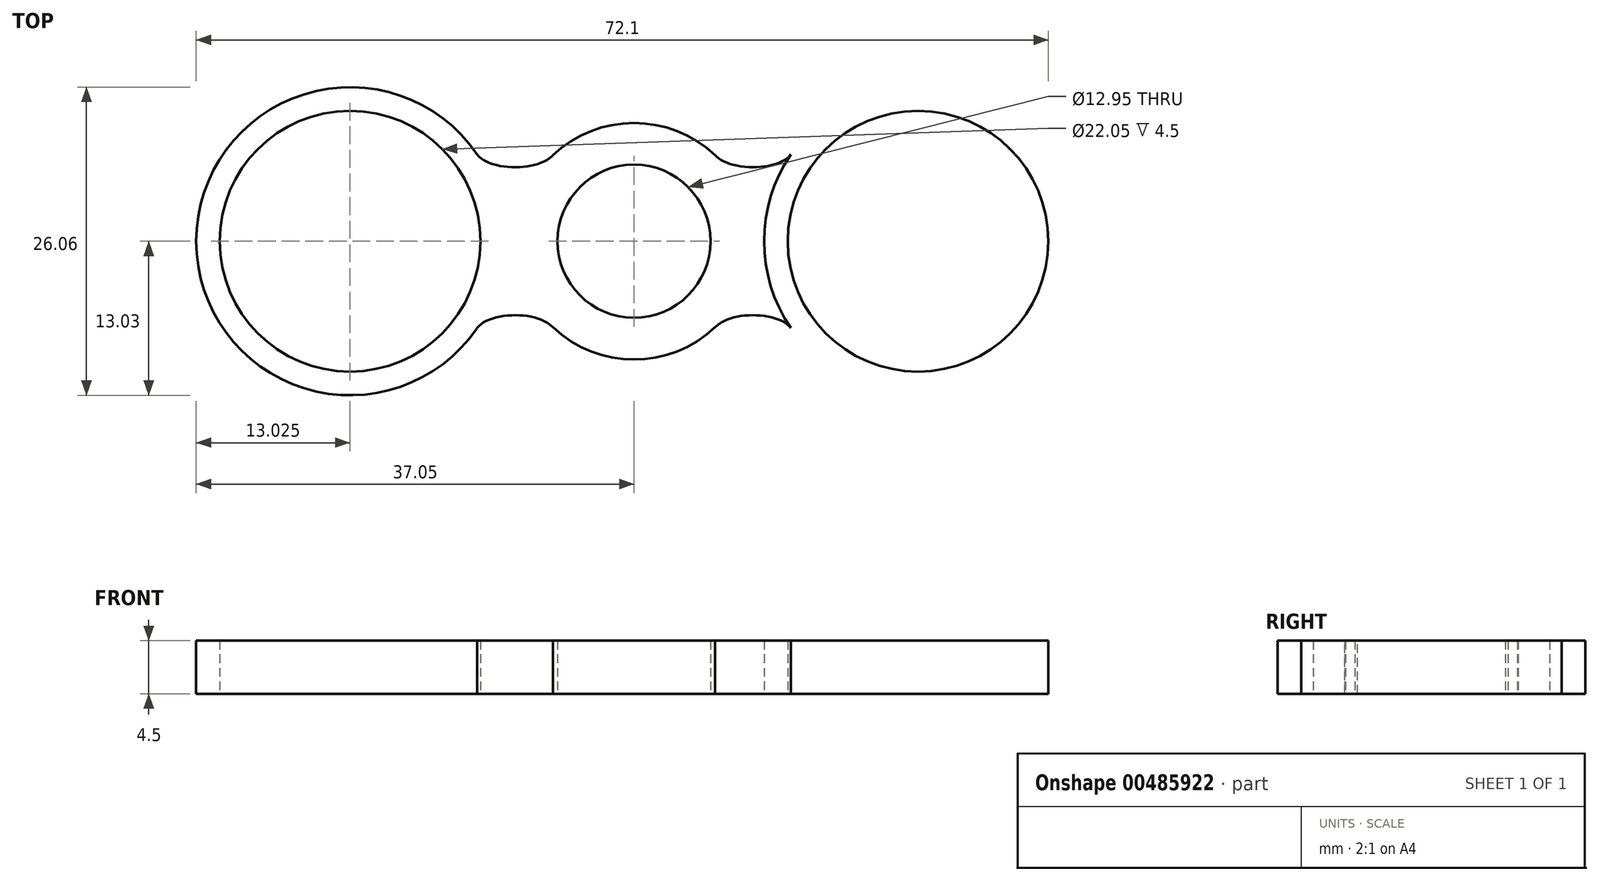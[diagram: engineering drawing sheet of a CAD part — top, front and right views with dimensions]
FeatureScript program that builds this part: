
annotation { "Feature Type Name" : "Feature", "Feature Type Description" : "" }
export const myFeature = defineFeature(function(context is Context, id is Id, definition is map)
    precondition{}
    {
        {
            var Q0;
            Q0=qCreatedBy(makeId("Top.planeOp"),FACE);
            var sketch = newSketch(context, id + "F0", { "sketchPlane" : qUnion([Q0])});
            skCircle(sketch, "E0", {"center": v(0, 0) * mm, "radius": 8 * mm});
            skCircle(sketch, "E1", {"center": v(0, 0) * mm, "radius": 6.47 * mm});
            skCircle(sketch, "E2", {"center": v(-24.03, 0) * mm, "radius": 11.03 * mm});
            skCircle(sketch, "E3.MirrorC", {"center": v(24.03, 0) * mm, "radius": 11.03 * mm});
            skCircle(sketch, "E4.0", {"center": v(-24.03, 0) * mm, "radius": 13.03 * mm});
            skCircle(sketch, "E5.0", {"center": v(0, 0) * mm, "radius": 10 * mm});
            skCircle(sketch, "E6.0", {"center": v(24.03, 0) * mm, "radius": 13.03 * mm});
            skFitSpline(sketch, "E7", {"points": [v(-13.3, 7.39) * mm, v(-10.25, 6.26) * mm, v(-6.87, 7.27) * mm], "startDerivative": vector(2.88, -4.43) * mm, "endDerivative": vector(4.25, 4.27) * mm});
            skFitSpline(sketch, "E8.MirrorCS", {"points": [v(13.3, 7.39) * mm, v(10.25, 6.26) * mm, v(6.87, 7.27) * mm], "startDerivative": vector(-2.88, -4.43) * mm, "endDerivative": vector(-4.25, 4.27) * mm});
            skFitSpline(sketch, "E9.MirrorCS", {"points": [v(-13.3, -7.39) * mm, v(-10.25, -6.26) * mm, v(-6.87, -7.27) * mm], "startDerivative": vector(2.88, 4.43) * mm, "endDerivative": vector(4.25, -4.27) * mm});
            skFitSpline(sketch, "E10.MirrorCS", {"points": [v(13.3, -7.39) * mm, v(10.25, -6.26) * mm, v(6.87, -7.27) * mm], "startDerivative": vector(-2.88, 4.43) * mm, "endDerivative": vector(-4.25, -4.27) * mm});
            skSolve(sketch);
        }
        {
            var Q0;
            {var subQ0=sQuery(id+"F0.wireOp",EDGE,"11135997-ce24-4859-bc86-bf1433c228200.MirrorCS");Q0=makeQuery(id+"F0.imprint","IMPRINT",FACE,{"disambiguationData":[TD([[makeQuery(id+"F0.imprint","IMPRINT",EDGE,{"derivedFrom":subQ0}),1.0]])]});}
            var Q1;
            {var subQ0=sQuery(id+"F0.wireOp",EDGE,"D08EA6w1-EXNL-rs5g-QlH0-ys5wiicUSHVg.bottom");Q1=makeQuery(id+"F0.imprint","IMPRINT",FACE,{"disambiguationData":[TD([[makeQuery(id+"F0.imprint","IMPRINT",EDGE,{"derivedFrom":subQ0}),-1.0]])]});}
            var Q2;
            Q2=makeQuery(id+"F0.imprint","IMPRINT",FACE,{"disambiguationData":[TD([[makeQuery(id+"F0.imprint","IMPRINT",EDGE,{"derivedFrom":sQuery(id+"F0.wireOp",EDGE,"E1")}),-1.0]])]});
            var Q3;
            Q3=makeQuery(id+"F0.imprint","IMPRINT",FACE,{"disambiguationData":[TD([[makeQuery(id+"F0.imprint","IMPRINT",EDGE,{"derivedFrom":sQuery(id+"F0.wireOp",EDGE,"E0")}),-1.0]])]});
            extrude(context, id + "F1", {"entities" : qUnion([Q0, Q1, Q2, Q3]), "depth" : 4 * mm});
        }
        {
            var Q0;
            Q0=makeQuery(id+"F0.imprint","IMPRINT",FACE,{"disambiguationData":[TD([[makeQuery(id+"F0.imprint","IMPRINT",EDGE,{"derivedFrom":sQuery(id+"F0.wireOp",EDGE,"E0")}),1.0]])]});
            extrude(context, id + "F2", {"entities" : qUnion([Q0]), "operationType" : NewBodyOperationType.ADD, "depth" : 4.5 * mm});
        }
        {
            var Q0;
            Q0=makeQuery(id+"F1.opExtrude","CAP_FACE",FACE,{"disambiguationData":[OSD([sQuery(id+"F0.wireOp",EDGE,"E1"),sQuery(id+"F0.wireOp",EDGE,"E2"),sQuery(id+"F0.wireOp",EDGE,"E3.MirrorC"),sQuery(id+"F0.wireOp",EDGE,"GgWqVswa-p5QZ-sH4Y-k3uy-xwgDCf22LV1x.bottom"),sQuery(id+"F0.wireOp",EDGE,"GgWqVswa-p5QZ-sH4Y-k3uy-xwgDCf22LV1x.top"),sQuery(id+"F0.wireOp",EDGE,"GgWqVswa-p5QZ-sH4Y-k3uy-xwgDCf22LV1x.left"),sQuery(id+"F0.wireOp",EDGE,"GgWqVswa-p5QZ-sH4Y-k3uy-xwgDCf22LV1x.right"),sQuery(id+"F0.wireOp",EDGE,"422a6344-0ef6-4c7b-b4d4-3de755b36a86.filletArc"),sQuery(id+"F0.wireOp",EDGE,"f61ca1e3-e1b5-4427-8bb5-09bc14aa69ce.filletArc"),sQuery(id+"F0.wireOp",EDGE,"3ea78046-762b-468c-a92b-f7c5ba6cad61.filletArc"),sQuery(id+"F0.wireOp",EDGE,"a448e8b4-5851-43f8-8c25-36e1f7b4761f.filletArc")])],"isStart":false});
            var Q1;
            Q1=makeQuery(id+"F0.imprint","IMPRINT",FACE,{"disambiguationData":[TD([[makeQuery(id+"F0.imprint","IMPRINT",EDGE,{"derivedFrom":sQuery(id+"F0.wireOp",EDGE,"E2")}),-1.0]])]});
            var Q2;
            {var subQ0=sQuery(id+"F0.wireOp",EDGE,"E7");var subQ1=sQuery(id+"F0.wireOp",EDGE,"E4.0");var subQ2=makeQuery(id+"F0.imprint","INTERSECT",VERTEX,{"disambiguationData":[OD(1.0)],"derivedFrom":[subQ1,subQ0]});Q2=makeQuery(id+"F0.imprint","IMPRINT",FACE,{"disambiguationData":[TD([[makeQuery(id+"F0.imprint","IMPRINT",EDGE,{"disambiguationData":[TD([[subQ2,1.0]])],"derivedFrom":subQ1}),-1.0]])]});}
            var Q3;
            {var subQ0=sQuery(id+"F0.wireOp",EDGE,"E8.MirrorCS");var subQ1=sQuery(id+"F0.wireOp",EDGE,"E5.0");var subQ2=makeQuery(id+"F0.imprint","INTERSECT",VERTEX,{"disambiguationData":[OD(1.0)],"derivedFrom":[subQ1,subQ0]});Q3=makeQuery(id+"F0.imprint","IMPRINT",FACE,{"disambiguationData":[TD([[makeQuery(id+"F0.imprint","IMPRINT",EDGE,{"disambiguationData":[TD([[subQ2,1.0]])],"derivedFrom":subQ1}),-1.0]])]});}
            var Q4;
            Q4=makeQuery(id+"F0.imprint","IMPRINT",FACE,{"disambiguationData":[TD([[makeQuery(id+"F0.imprint","IMPRINT",EDGE,{"derivedFrom":sQuery(id+"F0.wireOp",EDGE,"E3.MirrorC")}),1.0]])]});
            var Q5;
            Q5=makeQuery(id+"F2.opExtrude","CAP_FACE",FACE,{"disambiguationData":[OSD([sQuery(id+"F0.wireOp",EDGE,"E0"),sQuery(id+"F0.wireOp",EDGE,"E1")])],"isStart":false});
            extrude(context, id + "F3", {"entities" : qUnion([Q0, Q1, Q2, Q3, Q4]), "operationType" : NewBodyOperationType.ADD, "endBound" : BoundingType.UP_TO_SURFACE, "endBoundEntityFace" : qUnion([Q5]), "depth" : 25 * mm});
        }
    });
